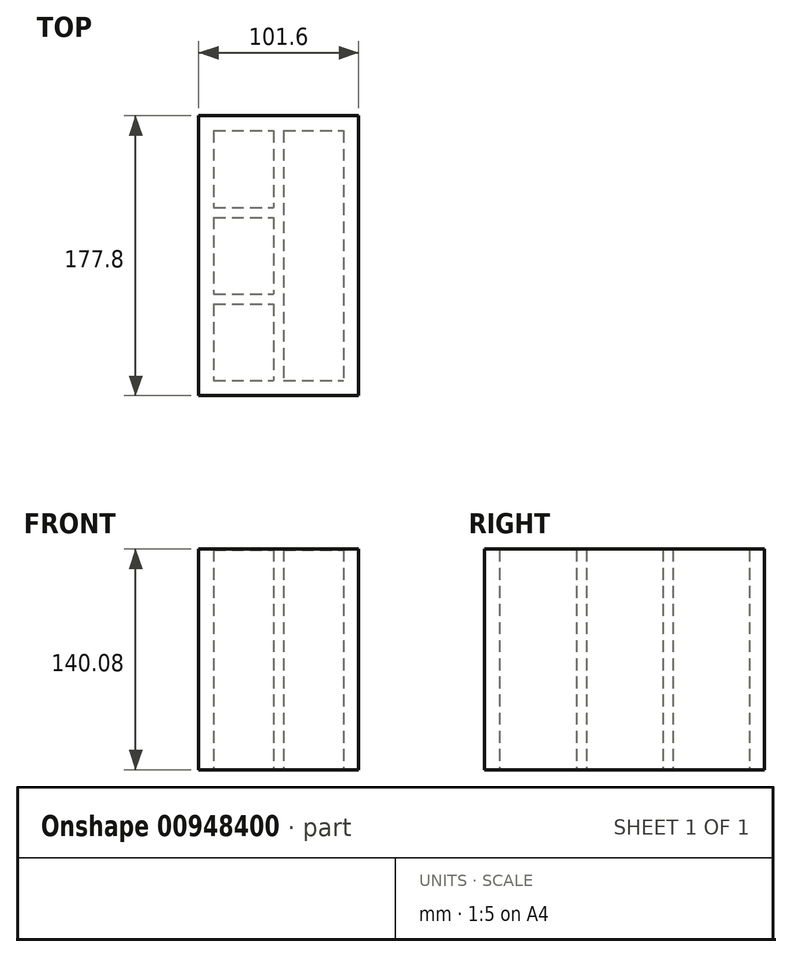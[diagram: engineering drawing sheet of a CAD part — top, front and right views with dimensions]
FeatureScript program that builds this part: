
annotation { "Feature Type Name" : "Feature", "Feature Type Description" : "" }
export const myFeature = defineFeature(function(context is Context, id is Id, definition is map)
    precondition{}
    {
        {
            assignVariable(context, id + "F0", {"name" : "outside_thickness", "anyValue" : 3 / 8});
        }
        {
            var Q0;
            Q0=qCreatedBy(makeId("Top.planeOp"),FACE);
            var sketch = newSketch(context, id + "F1", { "sketchPlane" : qUnion([Q0])});
            skLineSegment(sketch, "E0.bottom", {"start": v(0, 0) * mm, "end": v(101.6, 0) * mm});
            skLineSegment(sketch, "E0.top", {"start": v(0, 177.8) * mm, "end": v(101.6, 177.8) * mm});
            skLineSegment(sketch, "E0.left", {"start": v(0, 0) * mm, "end": v(0, 177.8) * mm});
            skLineSegment(sketch, "E0.right", {"start": v(101.6, 0) * mm, "end": v(101.6, 177.8) * mm});
            skLineSegment(sketch, "E1.bottom", {"start": v(53.97, 168.28) * mm, "end": v(92.07, 168.28) * mm});
            skLineSegment(sketch, "E1.top", {"start": v(53.97, 9.52) * mm, "end": v(92.08, 9.52) * mm});
            skLineSegment(sketch, "E1.left", {"start": v(53.98, 168.28) * mm, "end": v(53.98, 9.53) * mm});
            skLineSegment(sketch, "E1.right", {"start": v(92.08, 168.28) * mm, "end": v(92.08, 9.53) * mm});
            skLineSegment(sketch, "E2.bottom", {"start": v(9.52, 168.28) * mm, "end": v(47.62, 168.28) * mm});
            skLineSegment(sketch, "E2.top", {"start": v(9.52, 119.6) * mm, "end": v(47.63, 119.6) * mm});
            skLineSegment(sketch, "E2.left", {"start": v(9.53, 168.28) * mm, "end": v(9.53, 119.6) * mm});
            skLineSegment(sketch, "E2.right", {"start": v(47.63, 168.28) * mm, "end": v(47.63, 119.6) * mm});
            skLineSegment(sketch, "E3.bottom", {"start": v(9.52, 113.24) * mm, "end": v(47.63, 113.24) * mm});
            skLineSegment(sketch, "E3.top", {"start": v(9.52, 64.56) * mm, "end": v(47.63, 64.56) * mm});
            skLineSegment(sketch, "E3.left", {"start": v(9.53, 113.24) * mm, "end": v(9.53, 64.56) * mm});
            skLineSegment(sketch, "E3.right", {"start": v(47.63, 113.24) * mm, "end": v(47.63, 64.56) * mm});
            skLineSegment(sketch, "E4.bottom", {"start": v(9.52, 58.2) * mm, "end": v(47.63, 58.2) * mm});
            skLineSegment(sketch, "E4.top", {"start": v(9.53, 9.52) * mm, "end": v(50.92, 9.53) * mm});
            skLineSegment(sketch, "E4.left", {"start": v(9.53, 58.2) * mm, "end": v(9.53, 9.52) * mm});
            skLineSegment(sketch, "E4.right", {"start": v(47.63, 58.2) * mm, "end": v(47.63, 9.53) * mm});
            skLineSegment(sketch, "E5", {"start": v(50.8, 177.8) * mm, "end": v(50.92, 0) * mm, "construction": true});
            skLineSegment(sketch, "E6.bottom", {"start": v(47.62, 177.8) * mm, "end": v(53.97, 177.8) * mm, "construction": true});
            skLineSegment(sketch, "E6.top", {"start": v(47.63, 0) * mm, "end": v(53.97, 0) * mm, "construction": true});
            skLineSegment(sketch, "E6.left", {"start": v(47.63, 177.8) * mm, "end": v(47.63, 0) * mm, "construction": true});
            skLineSegment(sketch, "E6.right", {"start": v(53.98, 177.8) * mm, "end": v(53.98, 0) * mm, "construction": true});
            skLineSegment(sketch, "E7", {"start": v(28.58, 119.6) * mm, "end": v(28.58, 113.24) * mm, "construction": true});
            skLineSegment(sketch, "E8", {"start": v(28.58, 64.56) * mm, "end": v(28.58, 58.2) * mm, "construction": true});
            skLineSegment(sketch, "E9", {"start": v(9.53, 143.93) * mm, "end": v(0, 143.93) * mm, "construction": true});
            skLineSegment(sketch, "E10", {"start": v(73.03, 168.28) * mm, "end": v(73.03, 177.8) * mm, "construction": true});
            skLineSegment(sketch, "E11", {"start": v(92.07, 88.9) * mm, "end": v(101.6, 88.9) * mm, "construction": true});
            skLineSegment(sketch, "E12", {"start": v(73.03, 9.52) * mm, "end": v(73.03, 0) * mm, "construction": true});
            skSolve(sketch);
        }
        {
            var Q0;
            Q0 = qSketchRegion(id + "F1", true);
            extrude(context, id + "F2", {"entities" : qUnion([Q0]), "depth" : 139.7 * mm, "offsetDistance" : 25.4 * mm});
        }
        {
            var Q0;
            Q0=makeQuery(id+"F2.opExtrude","CAP_FACE",FACE,{"disambiguationData":[OSD([sQuery(id+"F1.wireOp",EDGE,"E0.bottom"),sQuery(id+"F1.wireOp",EDGE,"E0.top"),sQuery(id+"F1.wireOp",EDGE,"E0.left"),sQuery(id+"F1.wireOp",EDGE,"E0.right"),sQuery(id+"F1.wireOp",EDGE,"E1.bottom"),sQuery(id+"F1.wireOp",EDGE,"E1.top"),sQuery(id+"F1.wireOp",EDGE,"E1.left"),sQuery(id+"F1.wireOp",EDGE,"E1.right"),sQuery(id+"F1.wireOp",EDGE,"E2.bottom"),sQuery(id+"F1.wireOp",EDGE,"E2.top"),sQuery(id+"F1.wireOp",EDGE,"E2.left"),sQuery(id+"F1.wireOp",EDGE,"E2.right"),sQuery(id+"F1.wireOp",EDGE,"E3.bottom"),sQuery(id+"F1.wireOp",EDGE,"E3.top"),sQuery(id+"F1.wireOp",EDGE,"E3.left"),sQuery(id+"F1.wireOp",EDGE,"E3.right"),sQuery(id+"F1.wireOp",EDGE,"E4.bottom"),sQuery(id+"F1.wireOp",EDGE,"E4.top"),sQuery(id+"F1.wireOp",EDGE,"E4.left"),sQuery(id+"F1.wireOp",EDGE,"E4.right")])],"isStart":false});
            var sketch = newSketch(context, id + "F3", { "sketchPlane" : qUnion([Q0])});
            skLineSegment(sketch, "E13.bottom", {"start": v(0, 177.8) * mm, "end": v(101.6, 177.8) * mm});
            skLineSegment(sketch, "E13.top", {"start": v(0, 0) * mm, "end": v(101.6, 0) * mm});
            skLineSegment(sketch, "E13.left", {"start": v(0, 177.8) * mm, "end": v(0, 0) * mm});
            skLineSegment(sketch, "E13.right", {"start": v(101.6, 177.8) * mm, "end": v(101.6, 0) * mm});
            skSolve(sketch);
        }
        {
            var Q0;
            Q0 = qSketchRegion(id + "F3", true);
            extrude(context, id + "F4", {"entities" : qUnion([Q0]), "operationType" : NewBodyOperationType.ADD, "depth" : (getVariable(context, 'outside_thickness')) * mm, "offsetDistance" : 25.4 * mm});
        }
    });
